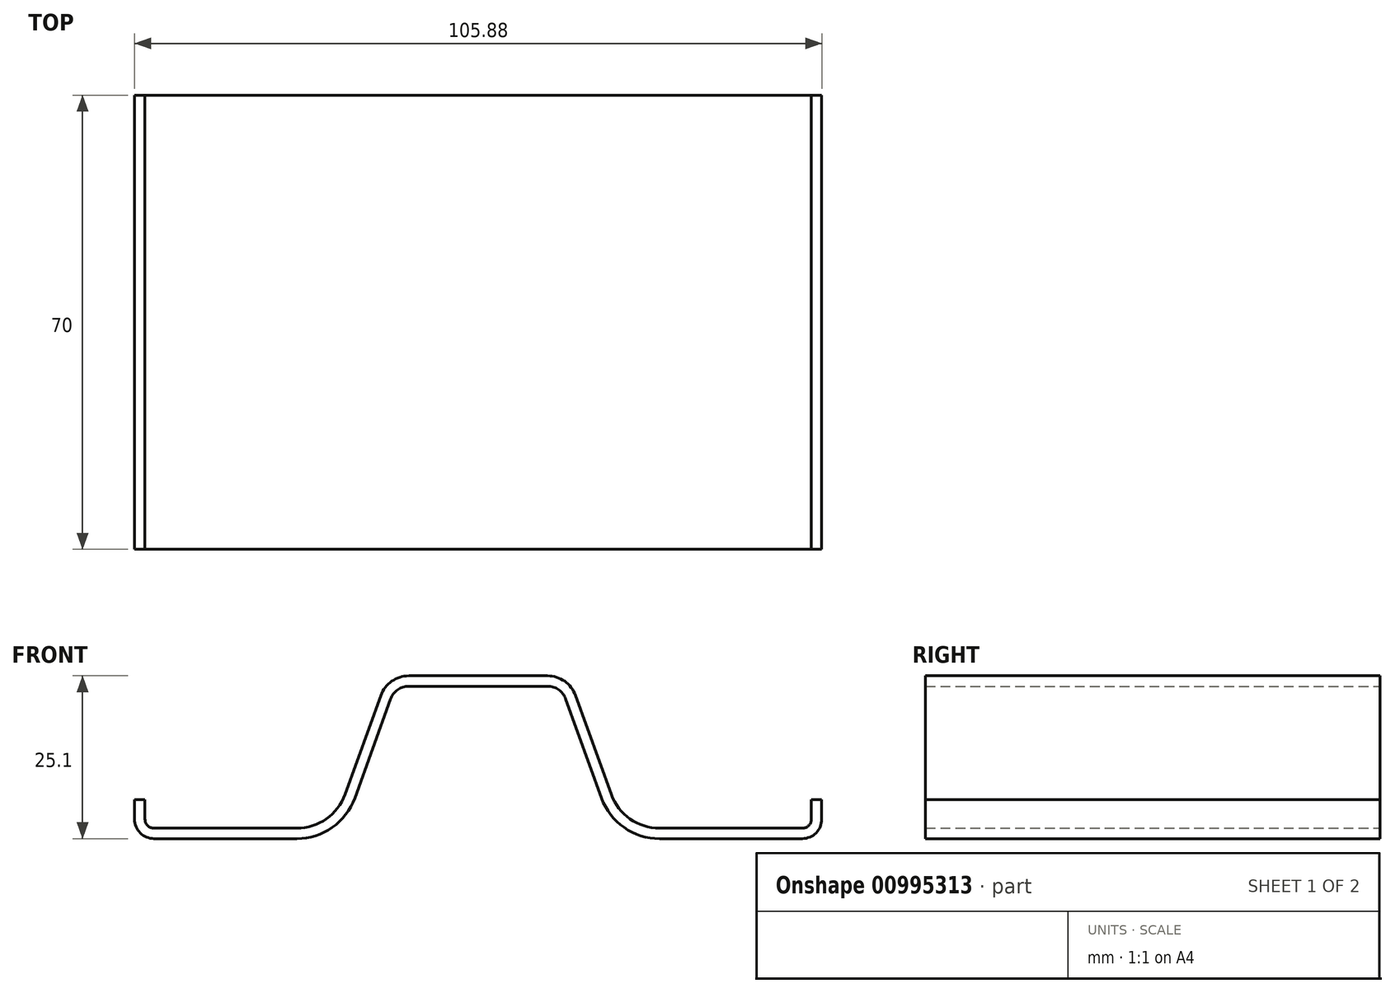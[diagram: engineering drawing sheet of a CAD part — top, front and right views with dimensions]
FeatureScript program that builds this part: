
annotation { "Feature Type Name" : "Feature", "Feature Type Description" : "" }
export const myFeature = defineFeature(function(context is Context, id is Id, definition is map)
    precondition{}
    {
        {
            var Q0;
            Q0=qCreatedBy(makeId("Front.planeOp"),FACE);
            var sketch = newSketch(context, id + "F0", { "sketchPlane" : qUnion([Q0])});
            skLineSegment(sketch, "E0", {"start": v(0, 23.5) * mm, "end": v(10.68, 23.5) * mm});
            skLineSegment(sketch, "E1", {"start": v(13.5, 21.52) * mm, "end": v(19, 6.28) * mm});
            skLineSegment(sketch, "E2", {"start": v(27.94, 0) * mm, "end": v(49.94, 0) * mm});
            skPoint(sketch, "E3.visualSharp", {"position": v(21.26, 0) * mm});
            skArc(sketch, "E3.filletArc", {"start": v(19, 6.28) * mm, "mid": v(22.48, 1.73) * mm, "end": v(27.94, 0) * mm});
            skPoint(sketch, "E4.visualSharp", {"position": v(12.78, 23.5) * mm});
            skArc(sketch, "E4.filletArc", {"start": v(13.5, 21.52) * mm, "mid": v(12.4, 22.96) * mm, "end": v(10.68, 23.5) * mm});
            skLineSegment(sketch, "E5", {"start": v(0, 0) * mm, "end": v(0, 23.5) * mm, "construction": true});
            skLineSegment(sketch, "E6", {"start": v(52.94, 3) * mm, "end": v(52.94, 6) * mm});
            skPoint(sketch, "E7.visualSharp", {"position": v(52.94, 0) * mm});
            skArc(sketch, "E7.filletArc", {"start": v(49.94, 0) * mm, "mid": v(52.06, 0.88) * mm, "end": v(52.94, 3) * mm});
            skLineSegment(sketch, "E8.0", {"start": v(51.34, 3) * mm, "end": v(51.34, 6) * mm});
            skArc(sketch, "E8.1", {"start": v(49.94, 1.6) * mm, "mid": v(50.93, 2.01) * mm, "end": v(51.34, 3) * mm});
            skLineSegment(sketch, "E8.2", {"start": v(27.94, 1.6) * mm, "end": v(49.94, 1.6) * mm});
            skLineSegment(sketch, "E8.3", {"start": v(0, 25.1) * mm, "end": v(10.68, 25.1) * mm});
            skArc(sketch, "E8.4", {"start": v(15, 22.06) * mm, "mid": v(13.32, 24.26) * mm, "end": v(10.68, 25.1) * mm});
            skLineSegment(sketch, "E8.5", {"start": v(15, 22.06) * mm, "end": v(20.5, 6.82) * mm});
            skArc(sketch, "E8.6", {"start": v(20.5, 6.82) * mm, "mid": v(23.4, 3.03) * mm, "end": v(27.94, 1.6) * mm});
            skLineSegment(sketch, "E9", {"start": v(51.34, 6) * mm, "end": v(52.94, 6) * mm});
            skLineSegment(sketch, "E10.MirrorCS", {"start": v(-51.34, 6) * mm, "end": v(-52.94, 6) * mm});
            skArc(sketch, "E11.MirrorCS", {"start": v(-49.94, 1.6) * mm, "mid": v(-50.93, 2.01) * mm, "end": v(-51.34, 3) * mm});
            skArc(sketch, "E12.MirrorCS", {"start": v(-13.5, 21.52) * mm, "mid": v(-12.4, 22.96) * mm, "end": v(-10.68, 23.5) * mm});
            skArc(sketch, "E13.MirrorCS", {"start": v(-15, 22.06) * mm, "mid": v(-13.32, 24.26) * mm, "end": v(-10.68, 25.1) * mm});
            skPoint(sketch, "E14.MirrorP", {"position": v(-52.94, 0) * mm});
            skLineSegment(sketch, "E15.MirrorCS", {"start": v(-52.94, 3) * mm, "end": v(-52.94, 6) * mm});
            skLineSegment(sketch, "E16.MirrorCS", {"start": v(-27.94, 0) * mm, "end": v(-49.94, 0) * mm});
            skPoint(sketch, "E17.MirrorP", {"position": v(-12.78, 23.5) * mm});
            skLineSegment(sketch, "E18.MirrorCS", {"start": v(-51.34, 3) * mm, "end": v(-51.34, 6) * mm});
            skArc(sketch, "E19.MirrorCS", {"start": v(-49.94, 0) * mm, "mid": v(-52.06, 0.88) * mm, "end": v(-52.94, 3) * mm});
            skLineSegment(sketch, "E20.MirrorCS", {"start": v(-15, 22.06) * mm, "end": v(-20.5, 6.82) * mm});
            skArc(sketch, "E21.MirrorCS", {"start": v(-20.5, 6.82) * mm, "mid": v(-23.4, 3.03) * mm, "end": v(-27.94, 1.6) * mm});
            skLineSegment(sketch, "E22.MirrorCS", {"start": v(0, 23.5) * mm, "end": v(-10.68, 23.5) * mm});
            skLineSegment(sketch, "E23.MirrorCS", {"start": v(-13.5, 21.52) * mm, "end": v(-19, 6.28) * mm});
            skArc(sketch, "E24.MirrorCS", {"start": v(-19, 6.28) * mm, "mid": v(-22.48, 1.73) * mm, "end": v(-27.94, 0) * mm});
            skLineSegment(sketch, "E25.MirrorCS", {"start": v(-27.94, 1.6) * mm, "end": v(-49.94, 1.6) * mm});
            skPoint(sketch, "E26.MirrorP", {"position": v(-21.26, 0) * mm});
            skLineSegment(sketch, "E27.MirrorCS", {"start": v(0, 25.1) * mm, "end": v(-10.68, 25.1) * mm});
            skSolve(sketch);
        }
        {
            var Q0;
            Q0 = qSketchRegion(id + "F0", true);
            extrude(context, id + "F1", {"entities" : qUnion([Q0]), "depth" : 70 * mm, "offsetDistance" : 25 * mm});
        }
    });
